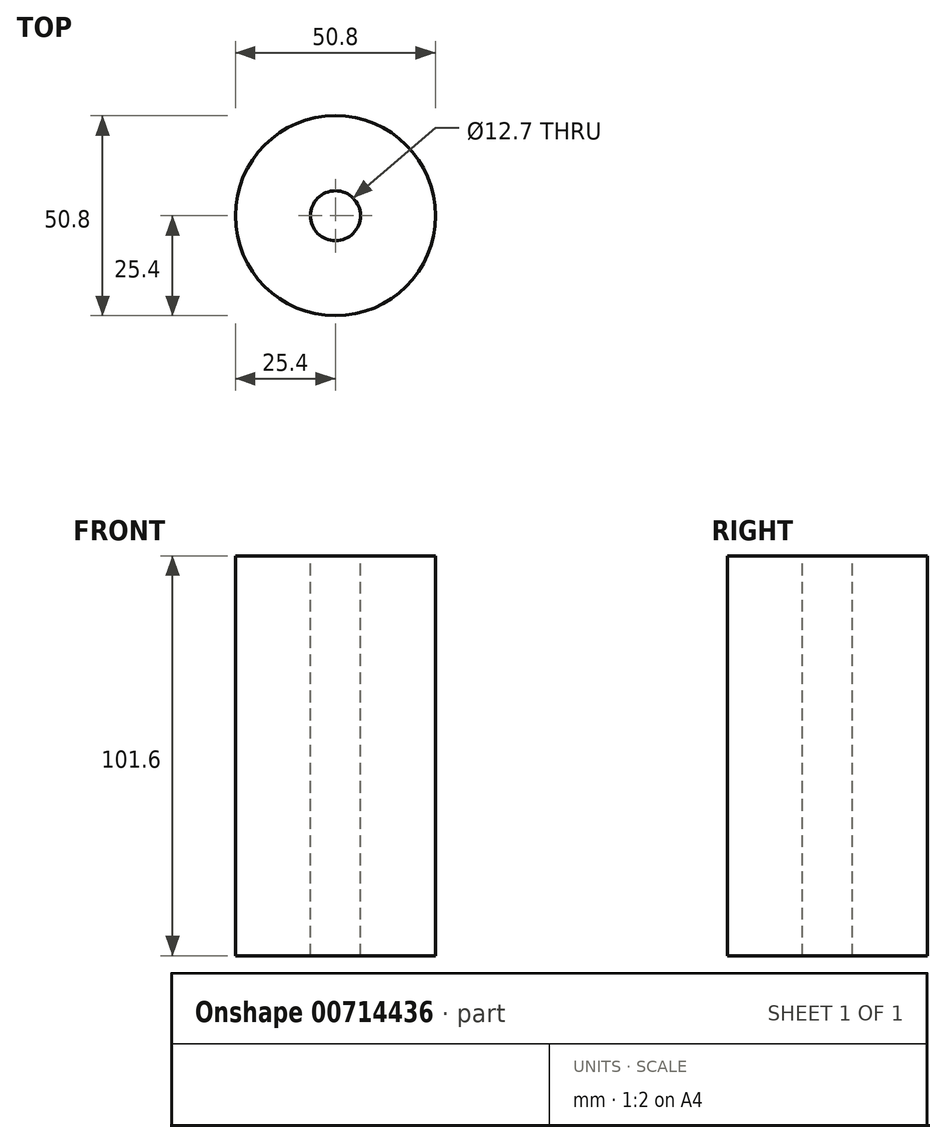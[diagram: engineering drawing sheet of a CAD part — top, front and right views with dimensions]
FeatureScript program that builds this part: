
annotation { "Feature Type Name" : "Feature", "Feature Type Description" : "" }
export const myFeature = defineFeature(function(context is Context, id is Id, definition is map)
    precondition{}
    {
        {
            var Q0;
            Q0=qCreatedBy(makeId("Top.planeOp"),FACE);
            var sketch = newSketch(context, id + "F0", { "sketchPlane" : qUnion([Q0])});
            skCircle(sketch, "E0", {"center": v(0, 0) * mm, "radius": 25.4 * mm});
            skCircle(sketch, "E1", {"center": v(0, 0) * mm, "radius": 6.35 * mm});
            skSolve(sketch);
        }
        {
            var Q0;
            Q0=qSketchRegion(id+"F0",true);
            extrude(context, id + "F1", {"entities" : qUnion([Q0]), "oppositeDirection" : true, "depth" : 101.6 * mm});
        }
    });
